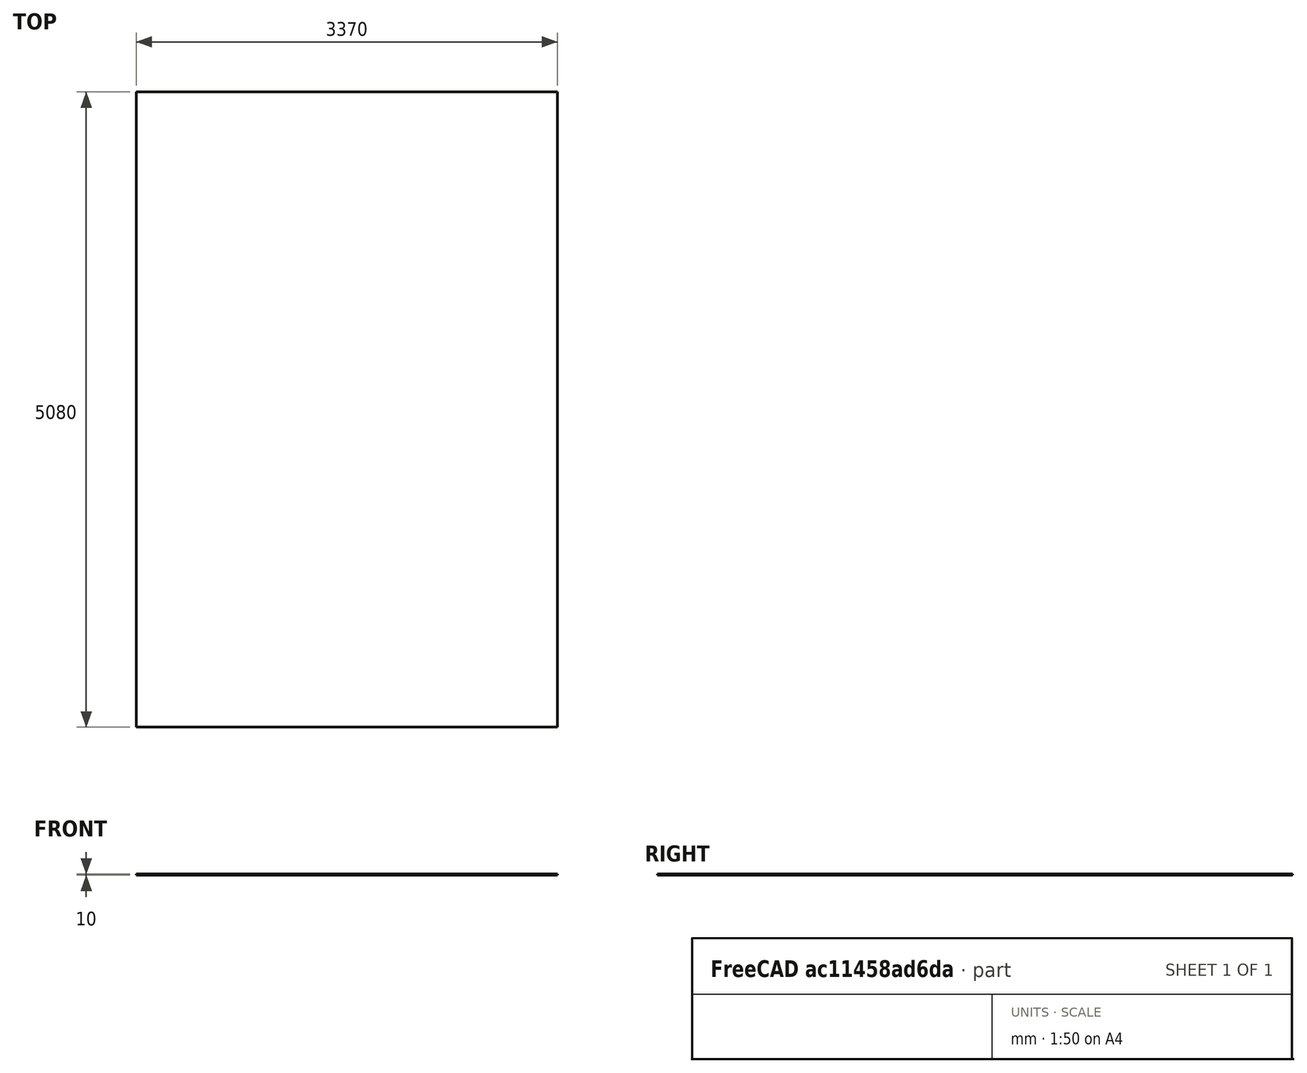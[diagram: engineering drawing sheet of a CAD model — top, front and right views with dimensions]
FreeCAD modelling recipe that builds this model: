
FCSTD DOCUMENT  (FreeCAD 0.19R24276 (Git))
Label: floor
License: All rights reserved
LicenseURL: http://en.wikipedia.org/wiki/All_rights_reserved
objects: Sketcher::SketchObject×1, PartDesign::Pad×1, PartDesign::Body×1
note: 4 computed .brp shape members not serialized (recipe doc carries the construction recipe); baked Part::Feature solids carry a one-line shape summary decoded from their .brp

FEATURE [Sketcher::SketchObject] Sketch
  FullyConstrained = true
  MapMode = 5
  Support = -> [XY_Plane]
  sketch-geometry (4):
    g0: LineSegment StartX=0 StartY=0 StartZ=0 EndX=3370 EndY=0 EndZ=0
    g1: LineSegment StartX=3370 StartY=0 StartZ=0 EndX=3370 EndY=-5080 EndZ=0
    g2: LineSegment StartX=3370 StartY=-5080 StartZ=0 EndX=0 EndY=-5080 EndZ=0
    g3: LineSegment StartX=0 StartY=-5080 StartZ=0 EndX=0 EndY=0 EndZ=0
  constraints (11):
    c: Coincident(g0,g1)
    c: Coincident(g1,g2)
    c: Coincident(g2,g3)
    c: Coincident(g3,g0)
    c: Horizontal(g0)
    c: Horizontal(g2)
    c: Vertical(g1)
    c: Vertical(g3)
    c: Coincident(g0,g-1)
    c: DistanceY(g3,g3) = 5080
    c: DistanceX(g0,g0) = 3370
FEATURE [PartDesign::Pad] Pad
  Direction = (1,1,1)
  Length = 10
  Length2 = 100
  Profile = -> Sketch
  Reversed = true
  Type = 0
FEATURE [PartDesign::Body] Body
  Group = -> [Sketch,Pad]
  Origin = -> Origin
  Tip = -> Pad
